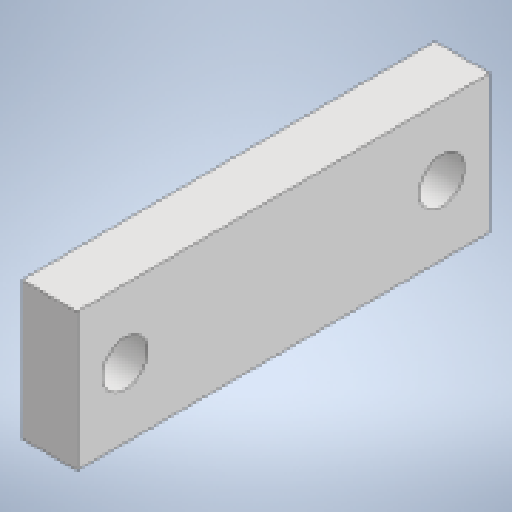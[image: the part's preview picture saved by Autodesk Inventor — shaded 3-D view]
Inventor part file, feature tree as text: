
AUTODESK INVENTOR PART (.ipt)
format: ipt  version: 2023 (Build 270158000, 158)  size: 124,928 bytes
history: native  units: mm
features: extrude x1, sketch x1
ambient origin geometry x8: Origin, YZ Plane, XZ Plane, XY Plane, X Axis, Y Axis, Z Axis, Center Point
bodies: Solid1 (feature_tree)
feature tree (2):
  extrude  "Extrusion1"  Depth=60.0mm
  sketch  "Sketch1"  dims[d0=20.0mm d1=60.0mm d2=6.6mm d3=6.6mm d4=46.0mm d5=10.0mm d6=7.0mm d7=8.0mm d8=0.0mm]
